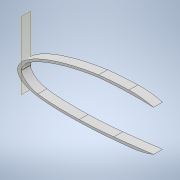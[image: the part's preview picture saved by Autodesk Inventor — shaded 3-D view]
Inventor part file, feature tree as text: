
AUTODESK INVENTOR PART (.ipt)
format: ipt  version: 2022.1 (Build 261234020, 234B)  size: 581,120 bytes
history: native  units: mm
features: sketch x7, extrude x6, thicken_offset x4, fillet x3, projected_geometry x3, shell x1, plane x1, other x1
ambient origin geometry x8: Origin, YZ Plane, XZ Plane, XY Plane, X Axis, Y Axis, Z Axis, Center Point
bodies: Solid1 (feature_tree)
feature tree (26):
  extrude  "Extrusion1"  Depth=10.0mm
  shell  "Shell1"  Thickness=1.0mm
  thicken_offset  "Thicken1"
  extrude  "Extrusion27"  TaperAngle=0.0deg  [1 undecoded]
  thicken_offset  "Thicken3"
  extrude  "Extrusion29"  Depth=20.0mm
  plane  "Work Plane5"
  other  "Bend Part2"
  thicken_offset  "Thicken5"
  extrude  "Extrusion30"  Depth=10.0mm TaperAngle=0.0deg
  extrude  "Extrusion31"  Depth=100.0mm
  fillet  "Fillet6"  Radius=1.0mm
  fillet  "Fillet7"  Radius=100.0mm
  thicken_offset  "Thicken6"
  extrude  "Extrusion32"  Depth=10.0mm TaperAngle=0.0deg
  fillet  "Fillet8"  Radius=150.0mm
  sketch  "Sketch3"  dims[d0=10.0mm d1=0.0mm d2=3.0mm d159=1.0mm d160=2.0mm]
  sketch  "Sketch48"  dims[d236=190.0mm d237=0.0mm d238=0.0mm]
  sketch  "Sketch55"  dims[d249=2.0mm d250=1.0mm d254=20.0mm]
  projected_geometry  "Projected Loop32"
  sketch  "Sketch57"  dims[d255=8.0mm d256=10.0mm d257=0.0mm]
  sketch  "Sketch58"  dims[d262=10.0mm d263=0.349066mm d264=1.0mm d265=1.0mm d268=100.0mm]
  projected_geometry  "Projected Loop34"
  sketch  "Sketch59"  dims[d269=5.0mm d270=10.0mm d271=0.0mm d272=150.0mm]
  sketch  "Sketch60"  dims[d273=100.0mm d274=0.0mm d275=550.0mm d276=100.0mm d277=6.0mm d278=2000.0mm d279=500.0mm d280=200.0mm d281=2.5mm d282=2.0mm d283=3.0mm d284=450.0mm d285=3.0mm d287=800.0mm d288=10.0mm d289=0.0mm d290=100.0mm]
  projected_geometry  "Projected Loop35"
note: 1 required parameter value undecoded (feature->parameter linkage not recoverable at this tier; creation-order binding heuristic only, values carry confidence <= 0.55)
